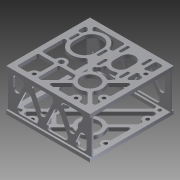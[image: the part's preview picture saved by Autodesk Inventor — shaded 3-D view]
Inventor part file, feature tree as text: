
AUTODESK INVENTOR PART (.ipt)
format: ipt  version: 2012 (Build 160160000, 160)  size: 909,824 bytes
history: native  units: in
note: dims shown in document units (in); Inventor stores cm internally (conversion verified against a paired STEP export)
features: thread x8, extrude x7, sketch x5, fillet x3, projected_geometry x1
ambient origin geometry x8: Origin, YZ Plane, XZ Plane, XY Plane, X Axis, Y Axis, Z Axis, Center Point
bodies: Solid1 (feature_tree)
feature tree (24):
  extrude  "Extrusion1"  Depth=0.1875in
  sketch  "Sketch2"  dims[d4=0.25in d5=0.25in d6=6.0in d7=0.0in]
  extrude  "Extrusion2"  Depth=6.0in TaperAngle=0.0deg
  extrude  "Extrusion3"  Depth=1.25in
  extrude  "Extrusion4"  Depth=1.625in
  fillet  "Fillet2"  Radius=0.375in
  sketch  "Sketch6"  dims[d20=0.25in d21=0.125in d22=0.25in d24=0.25in d25=0.125in d27=0.125in d32=0.25in d33=0.0in d35=0.375in d36=0.375in d37=0.375in d38=0.375in d39=0.1719in d40=0.3438in d41=0.3438in d42=0.3438in d43=0.3438in d44=0.125in d46=0.125in d49=0.125in d50=0.125in d51=0.125in d52=0.125in d53=0.125in d54=0.125in d55=0.125in d56=0.125in d57=0.25in d58=0.0in d60=0.3798in d61=0.287in d62=0.287in d63=0.287in d64=0.125in d65=0.125in d66=0.125in d67=0.125in d68=0.125in d69=0.125in d70=0.125in d71=0.125in d72=0.125in d73=0.125in d74=0.375in d76=0.25in d77=0.375in d78=0.375in d79=0.25in d80=0.0in d81=0.25in d88=0.125in d89=1.25in d90=1.5in d91=0.75in d92=0.5in d94=0.2in d96=0.9in d97=1.0in d98=0.5in d99=0.5in d101=2.0in d102=0.2in d103=0.8in d104=0.8in d105=0.7874in d107=1.6in d108=0.7874in d110=1.6in d114=1.0in d115=1.0in d116=1.625in d117=1.0in d119=0.2in d122=4.5in d123=1.3125in d124=0.366in d126=2.3in d127=0.25in d128=0.0in d129=0.375in d131=4.5in d132=0.125in d153=0.25in d154=0.125in d156=0.375in d157=0.375in d160=0.25in d161=0.125in d162=0.25in d163=0.125in d165=0.875in d166=0.125in d169=0.25in d170=0.125in d171=1.0in d172=0.25in d177=0.125in d178=0.6in d179=0.25in d180=0.0in d181=0.125in d183=0.25in d185=0.25in d186=0.125in d188=1.5625in d190=1.3125in d191=0.366in d193=0.25in d194=0.125in d197=1.0in d198=1.176in d199=0.1in d200=0.0in d201=0.125in d203=0.25in d204=0.25in d205=0.125in d207=2.1875in d208=2.0312in d211=0.125in d212=0.3in d213=0.5in d214=0.25in d215=0.3125in d220=0.5in d221=1.5in d222=0.25in d224=0.1875in d225=2.3in d226=0.35in d227=0.25in d228=1.5in d229=1.5in d230=0.5821in d231=0.25in d232=1.5in d233=0.125in d234=0.25in d235=2.0in d236=0.25in d237=1.5in d238=0.3125in d239=0.7874in d241=3.0in d242=0.3937in d244=1.0in d246=1.5in d247=0.7874in d249=3.0in d250=0.3937in d252=1.0in d254=0.5in d255=0.25in d256=0.3125in d257=0.25in d258=0.5in d259=0.3125in d260=0.25in d262=0.75in d264=6.0in d267=0.25in d269=3.0in d270=6.0in d272=0.25in d273=0.125in d274=0.125in d275=0.1435in d276=2.0in d277=1.0in d278=0.0in d279=1.0in d280=0.0in d281=1.0in d282=0.0in d283=1.0in d284=0.0in d285=1.0in d286=0.0in d287=1.0in d288=0.0in d289=1.0in d290=0.0in d291=1.0in d292=0.0in d293=0.125in d294=0.125in d295=0.125in d296=0.75in d297=0.4837in d298=0.375in]
  fillet  "Fillet3"  Radius=0.875in
  extrude  "Extrusion5"  Depth=0.125in
  extrude  "Extrusion6"  Depth=0.25in
  fillet  "Fillet4"  Radius=0.25in
  extrude  "Extrusion7"  Depth=0.125in
  thread  "Thread1"  [1 undecoded]
  thread  "Thread2"  [1 undecoded]
  thread  "Thread3"  [1 undecoded]
  thread  "Thread4"  [1 undecoded]
  thread  "Thread5"  [1 undecoded]
  thread  "Thread6"  [1 undecoded]
  thread  "Thread7"  [1 undecoded]
  thread  "Thread8"  [1 undecoded]
  sketch  "Sketch1"  dims[d1=3.0in d2=0.1875in d3=0.25in]
  sketch  "Sketch4"  dims[d11=2.0312in d13=1.25in]
  sketch  "Sketch5"  dims[d15=2.625in d16=1.625in d18=0.375in d19=0.875in]
  projected_geometry  "Projected Loop1"
note: 8 required parameter values undecoded (feature->parameter linkage not recoverable at this tier; creation-order binding heuristic only, values carry confidence <= 0.55)
